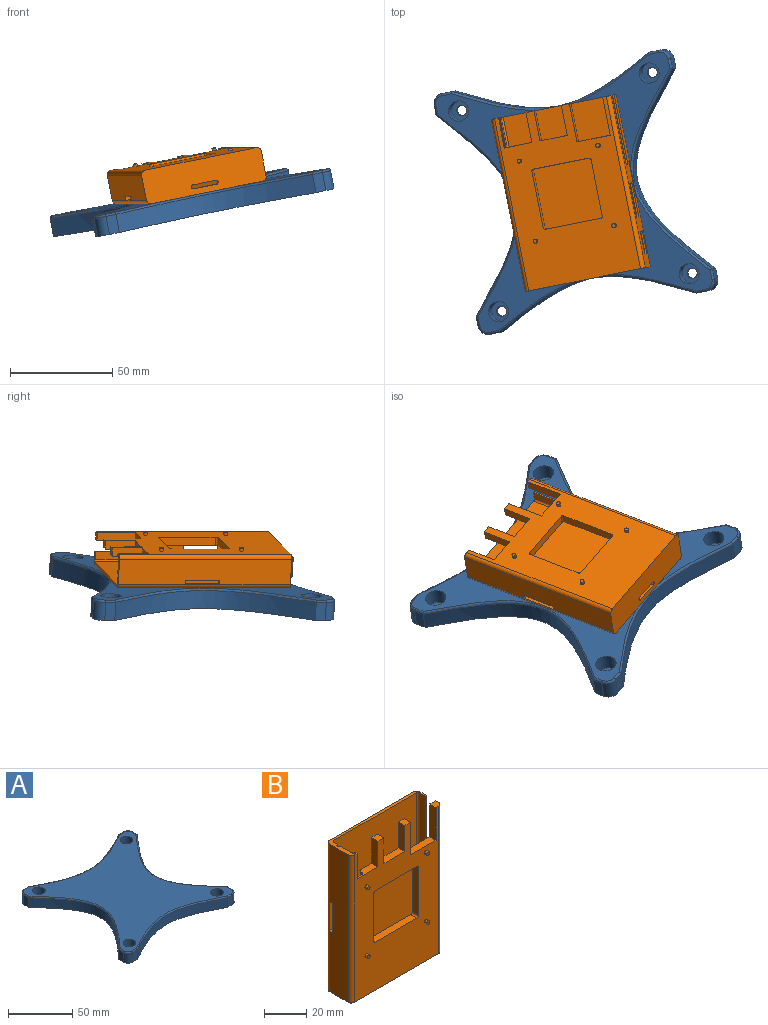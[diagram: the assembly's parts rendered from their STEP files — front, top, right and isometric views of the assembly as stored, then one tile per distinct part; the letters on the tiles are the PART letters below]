
ASSEMBLY  parts=2 mates=1
PART A: 46 faces, bbox 133.1x123x10 mm
  f0: plane 118.03x118.02mm, normal (0,0,1), area 7691.8mm2, adj f18,f20,f22,f24,f30,f31,f32,f33
  f1: plane 9x5mm, normal (0,-1,0), area 45mm2, adj f5,f13,f17,f42
  f2: plane 9x5mm, normal (1,0,0), area 45mm2, adj f5,f12,f15,f37
  f3: plane 9x5mm, normal (0,1,0), area 45mm2, adj f5,f11,f16,f30
  f4: plane 9x5mm, normal (-1,0,0), area 45mm2, adj f5,f10,f16,f34
  f5: plane 120x120mm, normal (0,0,-1), area 8445.9mm2, adj f1,f2,f3,f4,f6,f7,f8,f9
  f6: plane 9x5mm, normal (0,-1,0), area 45mm2, adj f5,f13,f14,f45
  f7: plane 9x5mm, normal (1,0,0), area 45mm2, adj f5,f12,f14,f41
  f8: plane 9x5mm, normal (0,1,0), area 45mm2, adj f5,f11,f15,f33
  f9: plane 9x5mm, normal (-1,0,0), area 45mm2, adj f5,f10,f17,f38
  f10: extruded ~100x29.6mm, area 1068.1mm2, adj f4,f5,f9,f36
  f11: extruded ~100x17.1mm, area 960.9mm2, adj f3,f5,f8,f31
  f12: extruded ~100x29.6mm, area 1067.3mm2, adj f2,f5,f7,f39
  f13: extruded ~100x17.1mm, area 960.5mm2, adj f1,f5,f6,f44
  f14: cylinder r=5mm len=9mm, axis (0,0,1), area 70.7mm2, adj f5,f6,f7,f43
  f15: cylinder r=5mm len=9mm, axis (0,0,-1), area 70.7mm2, adj f2,f5,f8,f35
  f16: cylinder r=5mm len=9mm, axis (0,0,1), area 70.7mm2, adj f3,f4,f5,f32
  f17: cylinder r=5mm len=9mm, axis (0,0,-1), area 70.7mm2, adj f1,f5,f9,f40
  f18: cylinder r=5mm len=10mm, axis (0,0,1), area 251.3mm2, adj f0,f19
  f19: plane 10x10mm, normal (0,0,1), area 58.9mm2, adj f18,f29
  f20: cylinder r=5mm len=10mm, axis (0,0,1), area 251.3mm2, adj f0,f21
  f21: plane 10x10mm, normal (0,0,1), area 58.9mm2, adj f20,f28
  f22: cylinder r=5mm len=10mm, axis (0,0,1), area 251.3mm2, adj f0,f23
  f23: plane 10x10mm, normal (0,0,1), area 58.9mm2, adj f22,f27
  f24: cylinder r=5mm len=10mm, axis (0,0,1), area 251.3mm2, adj f0,f25
  f25: plane 10x10mm, normal (0,0,1), area 58.9mm2, adj f24,f26
  f26: cylinder r=2.5mm len=5mm, axis (0,0,1), area 31.4mm2, adj f5,f25
  f27: cylinder r=2.5mm len=5mm, axis (0,0,1), area 31.4mm2, adj f5,f23
  f28: cylinder r=2.5mm len=5mm, axis (0,0,1), area 31.4mm2, adj f5,f21
  f29: cylinder r=2.5mm len=5mm, axis (0,0,1), area 31.4mm2, adj f5,f19
  f30: cylinder r=1mm len=5mm, axis (1,0,0), area 7.7mm2, adj f0,f3,f31,f32
  f31: bspline ~106.39x19.75mm, area 167.9mm2, adj f0,f11,f30,f33
  f32: torus R=4mm, axis (0,0,1), area 11.4mm2, adj f0,f16,f30,f34
  f33: cylinder r=1mm len=5mm, axis (1,0,0), area 7.7mm2, adj f0,f8,f31,f35
  f34: cylinder r=1mm len=5mm, axis (0,1,0), area 7.6mm2, adj f0,f4,f32,f36
  f35: torus R=4mm, axis (0,0,1), area 11.4mm2, adj f0,f15,f33,f37
  f36: bspline ~113.65x39.88mm, area 186.6mm2, adj f0,f10,f34,f38
  f37: cylinder r=1mm len=5mm, axis (0,-1,0), area 7.6mm2, adj f0,f2,f35,f39
  f38: cylinder r=1mm len=5mm, axis (0,1,0), area 7.6mm2, adj f0,f9,f36,f40
  f39: bspline ~106.61x34.43mm, area 186.5mm2, adj f0,f12,f37,f41
  f40: torus R=4mm, axis (0,0,1), area 11.4mm2, adj f0,f17,f38,f42
  f41: cylinder r=1mm len=5mm, axis (0,-1,0), area 7.6mm2, adj f0,f7,f39,f43
  f42: cylinder r=1mm len=5mm, axis (-1,0,0), area 7.7mm2, adj f0,f1,f40,f44
  f43: torus R=4mm, axis (0,0,1), area 11.4mm2, adj f0,f14,f41,f45
  f44: bspline ~105.43x19.48mm, area 167.8mm2, adj f0,f13,f42,f45
  f45: cylinder r=1mm len=5mm, axis (-1,0,0), area 7.7mm2, adj f0,f6,f43,f44
PART B: 85 faces, bbox 60.8x18.2x85.8 mm
  f0: plane 60.8x16.7mm, normal (0,0,-1), area 985.8mm2, adj f3,f6,f13,f14,f45,f46,f47,f48
  f1: plane 58.7x14.2mm, normal (0,0,1), area 630.1mm2, adj f2,f4,f7,f11,f12,f15,f16,f57
  f2: plane 84x50.3mm, normal (0,1,0), area 2631.3mm2, adj f1,f6,f7,f8,f9,f10,f17,f19
  f3: plane 85.8x56.8mm, normal (0,-1,0), area 3220mm2, adj f0,f5,f8,f9,f10,f17,f18,f19
  f4: plane 84x7.5mm, normal (1,0,0), area 630mm2, adj f1,f5,f57,f72
  f5: plane 60.8x16.7mm, normal (0,0,1), area 130.8mm2, adj f3,f4,f6,f7,f11,f13,f14,f15
  f6: plane 85.8x12.7mm, normal (1,0,0), area 666.2mm2, adj f0,f2,f5,f8,f26,f28,f29,f30
  f7: plane 84x10mm, normal (-1,0,0), area 428.2mm2, adj f1,f2,f5,f26,f29,f30,f31,f32
  f8: plane 4.2x3.8mm, normal (0,0,1), area 15.1mm2, adj f2,f3,f6,f21,f45
  f9: plane 4.2x4mm, normal (0,0,1), area 16.8mm2, adj f2,f3,f17,f25
  f10: plane 4.2x4mm, normal (0,0,1), area 16.8mm2, adj f2,f3,f22,f24
  f11: plane 84x5mm, normal (0,1,0), area 352.5mm2, adj f1,f5,f18,f19,f72,f73
  f12: plane 69x1.2mm, normal (-1,0,0), area 82.8mm2, adj f1,f19,f73,f74
  f13: plane 85.8x56.8mm, normal (0,1,0), area 4873.4mm2, adj f0,f5,f46,f47
  f14: plane 85.8x12.7mm, normal (-1,0,0), area 1055.7mm2, adj f0,f5,f47,f48,f53,f55,f56
  f15: plane 84x55.5mm, normal (0,-1,0), area 4662mm2, adj f1,f5,f75,f76
  f16: plane 84x2.7mm, normal (1,0,0), area 201.3mm2, adj f1,f5,f53,f55,f56,f58,f75
  f17: plane 15x4.2mm, normal (-1,0,0), area 63mm2, adj f2,f3,f9,f19
  f18: plane 15x1mm, normal (1,0,0), area 15mm2, adj f3,f5,f11,f19
  f19: plane 14x4.2mm, normal (0,0,1), area 41.2mm2, adj f2,f3,f11,f12,f17,f18,f73,f74
  f20: plane 17x4.2mm, normal (0,0,1), area 71.4mm2, adj f2,f3,f21,f22
  f21: plane 19x4.2mm, normal (-1,0,0), area 79.8mm2, adj f2,f3,f8,f20
  f22: plane 19x4.2mm, normal (1,0,0), area 79.8mm2, adj f2,f3,f10,f20
  f23: plane 14x4.2mm, normal (0,0,1), area 58.8mm2, adj f2,f3,f24,f25
  f24: plane 15x4.2mm, normal (-1,0,0), area 63mm2, adj f2,f3,f10,f23
  f25: plane 15x4.2mm, normal (1,0,0), area 63mm2, adj f2,f3,f9,f23
  f26: plane 31.5x0.8mm, normal (0,-1,0), area 25.2mm2, adj f5,f6,f7,f36
  f27: plane 16.2x0.2mm, normal (1,0,0), area 3.2mm2, adj f2,f28,f41,f44
  f28: plane 15x1.25mm, normal (0,1,0), area 18.8mm2, adj f6,f27,f41,f44
  f29: plane 5x0.8mm, normal (0,0,1), area 4mm2, adj f6,f7,f41,f42
  f30: plane 15x0.8mm, normal (0,-1,0), area 12mm2, adj f6,f7,f42,f43
  f31: plane 5x0.8mm, normal (0,0,-1), area 4mm2, adj f6,f7,f43,f44
  f32: plane 9.5x0.8mm, normal (0,1,0), area 7.6mm2, adj f6,f7,f37,f40
  f33: plane 4x0.8mm, normal (0,0,1), area 3.2mm2, adj f6,f7,f37,f38
  f34: plane 9.5x0.8mm, normal (0,-1,0), area 7.6mm2, adj f6,f7,f38,f39
  f35: plane 4x0.8mm, normal (0,0,-1), area 3.2mm2, adj f6,f7,f39,f40
  f36: cylinder r=3mm len=6mm, axis (-1,0,0), area 7.5mm2, adj f2,f6,f7,f26
  f37: cylinder r=1mm len=1mm, axis (1,0,0), area 1.3mm2, adj f6,f7,f32,f33
  f38: cylinder r=1mm len=1mm, axis (-1,0,0), area 1.3mm2, adj f6,f7,f33,f34
  f39: cylinder r=1mm len=1mm, axis (1,0,0), area 1.3mm2, adj f6,f7,f34,f35
  f40: cylinder r=1mm len=1mm, axis (-1,0,0), area 1.3mm2, adj f6,f7,f32,f35
  f41: cylinder r=1mm len=1.25mm, axis (1,0,0), area 1.5mm2, adj f2,f6,f7,f27,f28,f29
  f42: cylinder r=1mm len=1mm, axis (-1,0,0), area 1.3mm2, adj f6,f7,f29,f30
  f43: cylinder r=1mm len=1mm, axis (1,0,0), area 1.3mm2, adj f6,f7,f30,f31
  f44: cylinder r=1mm len=1.25mm, axis (-1,0,0), area 1.5mm2, adj f2,f6,f7,f27,f28,f31
  f45: cylinder r=2mm len=85.8mm, axis (0,0,1), area 269.5mm2, adj f0,f3,f6,f8
  f46: cylinder r=2mm len=85.8mm, axis (0,0,-1), area 269.5mm2, adj f0,f5,f6,f13,f49
  f47: cylinder r=2mm len=85.8mm, axis (0,0,1), area 269.5mm2, adj f0,f5,f13,f14,f54
  f48: cylinder r=2mm len=85.8mm, axis (0,0,-1), area 269.5mm2, adj f0,f3,f5,f14
  f49: plane 17x0.93mm, normal (0,-1,0), area 15.9mm2, adj f46,f50,f52,f76
  f50: plane 2x0.93mm, normal (0,0,-1), area 1.6mm2, adj f6,f7,f49,f51,f76
  f51: plane 17x0.8mm, normal (0,1,0), area 13.6mm2, adj f6,f7,f50,f52
  f52: plane 2x0.93mm, normal (0,0,1), area 1.6mm2, adj f6,f7,f49,f51,f76
  f53: plane 17x2.5mm, normal (0,1,0), area 42.5mm2, adj f14,f16,f55,f56
  f54: plane 17x2.63mm, normal (0,-1,0), area 44.8mm2, adj f47,f55,f56,f75
  f55: plane 2.63x2mm, normal (0,0,1), area 5mm2, adj f14,f16,f53,f54,f75
  f56: plane 2.63x2mm, normal (0,0,-1), area 5mm2, adj f14,f16,f53,f54,f75
  f57: plane 84x0.2mm, normal (0,1,0), area 16.8mm2, adj f1,f4,f5,f59
  f58: plane 84x0.2mm, normal (0,-1,0), area 16.8mm2, adj f1,f5,f16,f59
  f59: cylinder r=1mm len=84mm, axis (0,0,1), area 263.9mm2, adj f1,f5,f57,f58
  f60: plane 28x4.2mm, normal (0,0,1), area 117.6mm2, adj f2,f3,f68,f71
  f61: plane 28x4.2mm, normal (-1,0,0), area 117.6mm2, adj f2,f3,f68,f69
  f62: plane 28x4.2mm, normal (0,0,-1), area 117.6mm2, adj f2,f3,f69,f70
  f63: plane 28x4.2mm, normal (1,0,0), area 117.6mm2, adj f2,f3,f70,f71
  f64: plane 11.5x1.8mm, normal (0,-1,0), area 20.7mm2, adj f0,f1,f66,f67
  f65: plane 11.5x1.8mm, normal (0,1,0), area 20.7mm2, adj f0,f1,f66,f67
  f66: cylinder r=1mm len=2mm, axis (0,0,1), area 5.7mm2, adj f0,f1,f64,f65
  f67: cylinder r=1mm len=2mm, axis (0,0,1), area 5.7mm2, adj f0,f1,f64,f65
  f68: cylinder r=1mm len=4.2mm, axis (0,-1,0), area 6.6mm2, adj f2,f3,f60,f61
  f69: cylinder r=1mm len=4.2mm, axis (0,1,0), area 6.6mm2, adj f2,f3,f61,f62
  f70: cylinder r=1mm len=4.2mm, axis (0,-1,0), area 6.6mm2, adj f2,f3,f62,f63
  f71: cylinder r=1mm len=4.2mm, axis (0,1,0), area 6.6mm2, adj f2,f3,f60,f63
  f72: cylinder r=1mm len=84mm, axis (0,0,-1), area 131.9mm2, adj f1,f4,f5,f11
  f73: cylinder r=1mm len=69mm, axis (0,0,1), area 108.4mm2, adj f1,f11,f12,f19
  f74: cylinder r=1mm len=69mm, axis (0,0,-1), area 108.4mm2, adj f1,f2,f12,f19
  f75: cylinder r=1mm len=84mm, axis (0,0,1), area 123mm2, adj f1,f5,f15,f16,f54,f55,f56
  f76: cylinder r=1mm len=84mm, axis (0,0,-1), area 123mm2, adj f1,f5,f7,f15,f49,f50,f52
  f77: cylinder r=0.95mm len=1.9mm, axis (0,1,0), area 9mm2, adj f3,f78
  f78: plane 1.9x1.9mm, normal (0,-1,0), area 2.8mm2, adj f77
  f79: cylinder r=0.95mm len=1.9mm, axis (0,1,0), area 9mm2, adj f3,f80
  f80: plane 1.9x1.9mm, normal (0,-1,0), area 2.8mm2, adj f79
  f81: cylinder r=0.95mm len=1.9mm, axis (0,1,0), area 9mm2, adj f3,f82
  f82: plane 1.9x1.9mm, normal (0,-1,0), area 2.8mm2, adj f81
  f83: cylinder r=0.95mm len=1.9mm, axis (0,1,0), area 9mm2, adj f3,f84
  f84: plane 1.9x1.9mm, normal (0,-1,0), area 2.8mm2, adj f83
PLACE A rot(axis=(0.07,-0.71,0.71),15.9deg) t=(8.39,1.44,-23.82)mm
PLACE B rot(axis=(-0.98,-0.2,0),90deg) t=(13.33,-41.34,-5.8)mm
MATE parallel A.f0 <-> B.f13  axis (-0.19,-0.04,0.98) through (6.56,1.06,-13.99)mm
